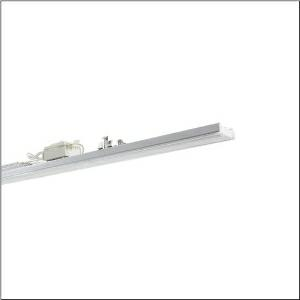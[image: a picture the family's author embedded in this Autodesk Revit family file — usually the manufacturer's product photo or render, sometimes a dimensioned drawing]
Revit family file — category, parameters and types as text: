
# Revit family: licross_r__21_recessed_mo_52tl18vn58xg_02ab
name_source: partatom
category: Lighting Fixtures
units: mm (PartAtom-declared; Revit-internal decimal feet)

## family parameters
Cut with Voids When Loaded = No
Host = Face
Light Source = No
Part Type = Normal
Room Calculation Point = No
Round Connector Dimension = Use Diameter
Shared = No

## types (1)
- --- (1 x LED, 8000 lm, 46.1 W, 5000K)
    Apparent Load = 46 VA
    CIE Flux Codes = 79 95 99 100 100
    Color Rendering = 80
    Color Temperature = 5000K
    Default Elevation = 1800 mm
    Description = Licross® 21 Recessed MO, luminaire insert, of sheet steel, galvanised, coil coated, white, length: 1.500mm, width: 66mm, height: 67mm, LED rated luminous flux: 8.000lm, light colour: 850, control gear: DALI 2, CLO, with plug, 5-pole, with phase selection, mains connection: 220..240V, AC, 50/60Hz, start of lifetime: 46W, end of service life: 55W, internal wiring halogen-free, primary optical cover: cover, of PMMA, light emission: direct distribution, primary light characteristic: symmetric, protection rating (complete): IP40, insulation class (complete): insulation class I (protective earthing), certification: CE, ENEC, VDE, UKCA, protection symbol: D if used in an environment without relevant dust loads with corresponding accessories, impact resistance: IK06, permissible ambient temperature for indoor applications: -25..+40°C, corresponds to IFS (International Featured Standards) requirements for safety and quality in the food industry, reducing of maximum allowable ambient temperature of 5°C with ceiling mounting, LABS conformity tested according to VDMA 24364:2018-05, packaging unit: 1 piece
    Height = 58 mm
    Lamp = 1 x LED
    Lamp Light Flux = 8000 lm
    Lamp Power = 46.1 W
    Lamp count = 1
    Length = 1500 mm
    Luminous efficacy = 174 lm/W
    Manufacturer = Siteco
    ModVariant = No
    Model = 52TL18VN58XG
    Mounting Place = Ceiling
    Mounting Type = Pendant
    Number of Poles = 1
    OnlyDefault = Yes
    Power Factor = 1
    Product Name = Licross® 21 Recessed MO
    Product group = luminaire insert | ceiling pendant
    ProductGroupID = 902
    Protection Class = Protection class I
    Protection Degree = IP 40
    RLX_Detail_Level = 1
    RLX_Emergency_Light_Flux = 0 lm
    RLX_Emergency_Type = 0
    RLX_Emergency_Type_DB = No
    RlxData = <blob elided: 24601 chars, md5=437bf9f4>
    Socket = socket
    Standby Power = 0 W
    System Light Flux = 8000 lm
    System Power = 46 W
    Type Comments = factory setting: luminous flux: 100 % | dim-lin: 254 | 310 mA
    Type Image = l_1296930.jpg
    URL = http://relux.com
    VarID = @adj_103675
    Voltage = 0 V
    Weight = 0.00 kg
    Width = 66 mm

## geometry (parser evidence)
native form markers: Blend x4, Sweep x12
no freeform markers — native parametric forms only
